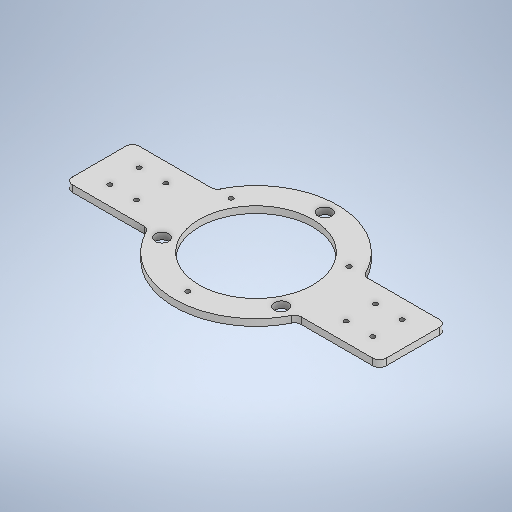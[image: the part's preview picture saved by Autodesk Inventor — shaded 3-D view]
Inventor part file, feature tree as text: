
AUTODESK INVENTOR PART (.ipt)
format: ipt  version: 2025 (Build 290162000, 162)  size: 313,856 bytes
history: native  units: in
note: dims shown in document units (in); Inventor stores cm internally (conversion verified against a paired STEP export)
features: sketch x5, hole x3, extrude x1, fillet x1, pattern_circular x1
ambient origin geometry x8: Origin, YZ Plane, XZ Plane, XY Plane, X Axis, Y Axis, Z Axis, Center Point
bodies: Solid1 (feature_tree)
feature tree (11):
  extrude  "Extrusion1"  Depth=0.1969in TaperAngle=0.0deg
  hole  "Hole1"  [1 undecoded]
  fillet  "Fillet2"  Radius=9.252in
  hole  "Pins"  [1 undecoded]
  hole  "Mounting Holes"  [1 undecoded]
  pattern_circular  "Circular Pattern1"  Count=2  [1 undecoded]
  sketch  "Sketch1"  dims[d0=3.3465in d3=0.1969in d4=0.0in]
  sketch  "Sketch2"  dims[d11=0.1276in d12=0.315in d13=0.1575in d14=0.0787in d15=90.0deg d16=0.4646in d17=0.8108in d29=2.4016in d46=9.252in]
  sketch  "Sketch4"  dims[d52=0.748in d53=0.5512in]
  sketch  "Sketch Circular Pattern2"  dims[d47=1.9685in d51=0.1575in]
  sketch  "Sketch5"  dims[d54=0.1575in d55=0.7874in d56=0.1969in d57=4.0551in d58=1.1811in d60=360.0deg d62=0.3937in d63=0.1181in d64=0.1575in d65=0.0787in d66=90.0deg d67=0.1181in d68=0.0in d69=4.0157in d70=0.1276in d71=0.315in d72=0.315in d73=0.2362in d74=90.0deg d75=0.315in d76=0.0in d77=1.1811in d78=360.0deg]
note: 4 required parameter values undecoded (feature->parameter linkage not recoverable at this tier; creation-order binding heuristic only, values carry confidence <= 0.55)
